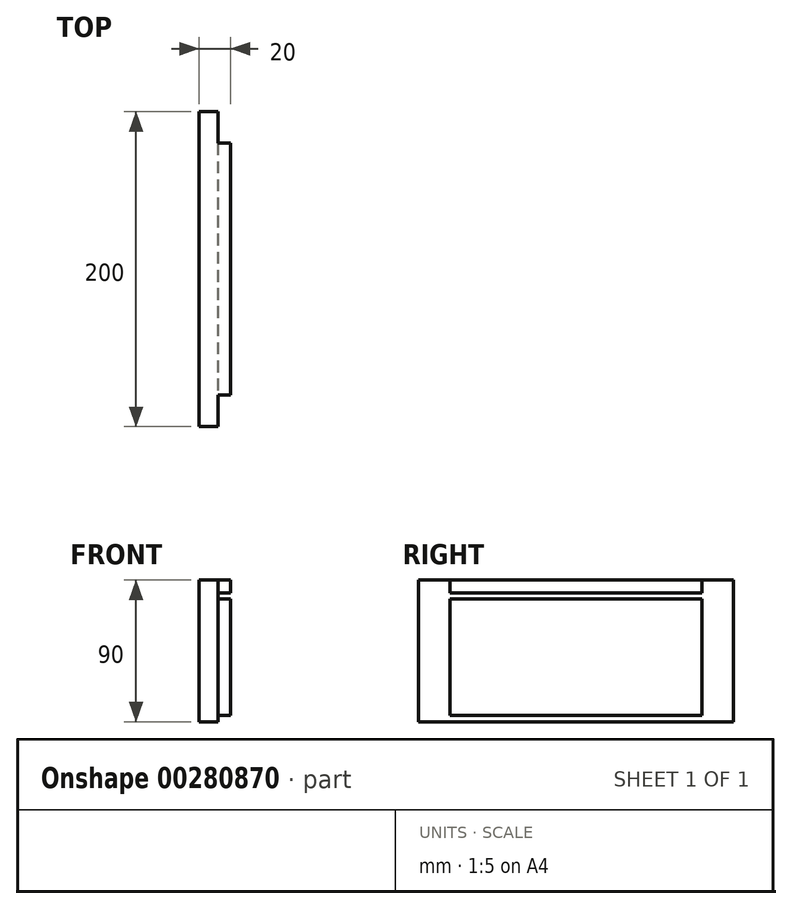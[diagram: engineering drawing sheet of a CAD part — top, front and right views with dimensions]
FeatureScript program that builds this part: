
annotation { "Feature Type Name" : "Feature", "Feature Type Description" : "" }
export const myFeature = defineFeature(function(context is Context, id is Id, definition is map)
    precondition{}
    {
        {
            var Q0;
            Q0=qCreatedBy(makeId("Top.planeOp"),FACE);
            var sketch = newSketch(context, id + "F0", { "sketchPlane" : qUnion([Q0])});
            skLineSegment(sketch, "E0.bottom", {"start": v(-9.72, 136.31) * mm, "end": v(10.28, 136.31) * mm});
            skLineSegment(sketch, "E0.top", {"start": v(-9.72, -63.69) * mm, "end": v(10.28, -63.69) * mm});
            skLineSegment(sketch, "E0.left", {"start": v(-9.72, 136.31) * mm, "end": v(-9.72, -63.69) * mm});
            skLineSegment(sketch, "E0.right", {"start": v(10.28, 136.31) * mm, "end": v(10.28, -63.69) * mm});
            skSolve(sketch);
        }
        {
            var Q0;
            Q0=makeQuery(id+"F0.imprint","IMPRINT",FACE,{"disambiguationData":[TD([[makeQuery(id+"F0.imprint","IMPRINT",EDGE,{"derivedFrom":sQuery(id+"F0.wireOp",EDGE,"E0.bottom")}),-1.0]])]});
            extrude(context, id + "F1", {"entities" : qUnion([Q0]), "depth" : 90 * mm});
        }
        {
            var Q0;
            Q0=makeQuery(id+"F1.opExtrude","CAP_FACE",FACE,{"disambiguationData":[OSD([sQuery(id+"F0.wireOp",EDGE,"E0.bottom"),sQuery(id+"F0.wireOp",EDGE,"E0.top"),sQuery(id+"F0.wireOp",EDGE,"E0.left"),sQuery(id+"F0.wireOp",EDGE,"E0.right")])],"isStart":false});
            var sketch = newSketch(context, id + "F2", { "sketchPlane" : qUnion([Q0])});
            skLineSegment(sketch, "E1.bottom", {"start": v(10.28, 136.31) * mm, "end": v(2.28, 136.31) * mm});
            skLineSegment(sketch, "E1.top", {"start": v(10.28, 116.31) * mm, "end": v(2.28, 116.31) * mm});
            skLineSegment(sketch, "E1.left", {"start": v(10.28, 136.31) * mm, "end": v(10.28, 116.31) * mm});
            skLineSegment(sketch, "E1.right", {"start": v(2.28, 136.31) * mm, "end": v(2.28, 116.31) * mm});
            skLineSegment(sketch, "E2.bottom", {"start": v(10.28, -63.69) * mm, "end": v(2.28, -63.69) * mm});
            skLineSegment(sketch, "E2.top", {"start": v(10.28, -43.69) * mm, "end": v(2.28, -43.69) * mm});
            skLineSegment(sketch, "E2.left", {"start": v(10.28, -63.69) * mm, "end": v(10.28, -43.69) * mm});
            skLineSegment(sketch, "E2.right", {"start": v(2.28, -63.69) * mm, "end": v(2.28, -43.69) * mm});
            skSolve(sketch);
        }
        {
            var Q0;
            Q0=makeQuery(id+"F2.imprint","IMPRINT",FACE,{"disambiguationData":[TD([[makeQuery(id+"F2.imprint","IMPRINT",EDGE,{"derivedFrom":sQuery(id+"F2.wireOp",EDGE,"E1.bottom")}),-1.0]])]});
            var Q1;
            Q1=makeQuery(id+"F2.imprint","IMPRINT",FACE,{"disambiguationData":[TD([[makeQuery(id+"F2.imprint","IMPRINT",EDGE,{"derivedFrom":sQuery(id+"F2.wireOp",EDGE,"E2.bottom")}),1.0]])]});
            extrude(context, id + "F3", {"entities" : qUnion([Q0, Q1]), "operationType" : NewBodyOperationType.REMOVE, "endBound" : BoundingType.UP_TO_NEXT, "oppositeDirection" : true, "depth" : 25 * mm});
        }
        {
            var Q0;
            Q0=makeQuery(id+"F3.boolean.opBoolean","COPY",FACE,{"derivedFrom":makeQuery(id+"F3.opExtrude","SWEPT_FACE",FACE,{"disambiguationData":[OSD([sQuery(id+"F2.wireOp",EDGE,"E2.top")])]})});
            var sketch = newSketch(context, id + "F4", { "sketchPlane" : qUnion([Q0])});
            skLineSegment(sketch, "E3.bottom", {"start": v(10.28, 82) * mm, "end": v(2.28, 82) * mm});
            skLineSegment(sketch, "E3.top", {"start": v(10.28, 78) * mm, "end": v(2.28, 78) * mm});
            skLineSegment(sketch, "E3.left", {"start": v(10.28, 82) * mm, "end": v(10.28, 78) * mm});
            skLineSegment(sketch, "E3.right", {"start": v(2.28, 82) * mm, "end": v(2.28, 78) * mm});
            skLineSegment(sketch, "E4.bottom", {"start": v(10.28, 0) * mm, "end": v(2.28, 0) * mm});
            skLineSegment(sketch, "E4.top", {"start": v(10.28, 4) * mm, "end": v(2.28, 4) * mm});
            skLineSegment(sketch, "E4.left", {"start": v(10.28, 0) * mm, "end": v(10.28, 4) * mm});
            skLineSegment(sketch, "E4.right", {"start": v(2.28, 0) * mm, "end": v(2.28, 4) * mm});
            skSolve(sketch);
        }
        {
            var Q0;
            Q0=makeQuery(id+"F4.imprint","IMPRINT",FACE,{"disambiguationData":[TD([[makeQuery(id+"F4.imprint","IMPRINT",EDGE,{"derivedFrom":sQuery(id+"F4.wireOp",EDGE,"E3.bottom")}),1.0]])]});
            var Q1;
            Q1=makeQuery(id+"F4.imprint","IMPRINT",FACE,{"disambiguationData":[TD([[makeQuery(id+"F4.imprint","IMPRINT",EDGE,{"derivedFrom":sQuery(id+"F4.wireOp",EDGE,"E4.bottom")}),1.0]])]});
            extrude(context, id + "F5", {"entities" : qUnion([Q0, Q1]), "operationType" : NewBodyOperationType.REMOVE, "endBound" : BoundingType.UP_TO_NEXT, "oppositeDirection" : true, "depth" : 25 * mm});
        }
    });
